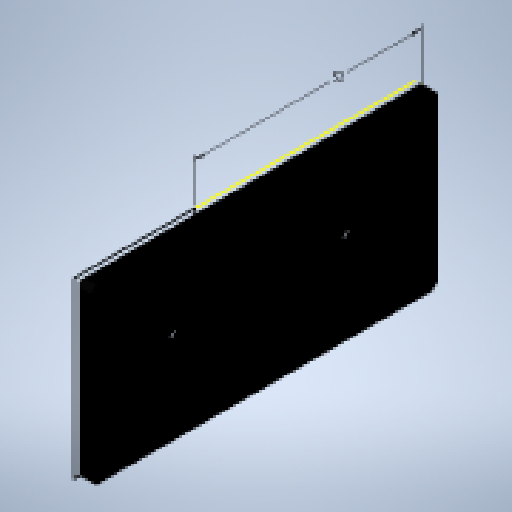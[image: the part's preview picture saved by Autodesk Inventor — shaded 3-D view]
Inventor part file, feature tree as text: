
AUTODESK INVENTOR PART (.ipt)
format: ipt  version: 2023 (Build 270158000, 158)  size: 273,920 bytes
history: native  units: mm
features: other x98, sketch x4, extrude x2, hole x2, chamfer x1
ambient origin geometry x8: Origin, YZ Plane, XZ Plane, XY Plane, X Axis, Y Axis, Z Axis, Center Point
bodies: Solid1 (feature_tree)
feature tree (107):
  extrude  "Extrusion1"  TaperAngle=0.0deg  [1 undecoded]
  hole  "Hole1"  [1 undecoded]
  hole  "Hole2"  [1 undecoded]
  other  "CS_ANBAU_CAP_XY"
  other  "CS_ANBAU_CAP_YZ"
  other  "CS_ANBAU_CAP_ZX"
  other  "CS_ANBAU_CAP_X"
  other  "CS_ANBAU_CAP_Y"
  other  "CS_ANBAU_CAP_Z"
  other  "CS_ANBAU_CAP_Center"
  other  "CS_ANBAU_CAP_90_XY"
  other  "CS_ANBAU_CAP_90_YZ"
  other  "CS_ANBAU_CAP_90_ZX"
  other  "CS_ANBAU_CAP_90_X"
  other  "CS_ANBAU_CAP_90_Y"
  other  "CS_ANBAU_CAP_90_Z"
  other  "CS_ANBAU_CAP_90_Center"
  other  "IB_1_XY"
  other  "IB_1_YZ"
  other  "IB_1_ZX"
  other  "IB_1_X"
  other  "IB_1_Y"
  other  "IB_1_Z"
  other  "IB_1_Center"
  other  "IB_10_XY"
  other  "IB_10_YZ"
  other  "IB_10_ZX"
  other  "IB_10_X"
  other  "IB_10_Y"
  other  "IB_10_Z"
  other  "IB_10_Center"
  other  "IB_11_XY"
  other  "IB_11_YZ"
  other  "IB_11_ZX"
  other  "IB_11_X"
  other  "IB_11_Y"
  other  "IB_11_Z"
  other  "IB_11_Center"
  other  "IB_12_XY"
  other  "IB_12_YZ"
  other  "IB_12_ZX"
  other  "IB_12_X"
  other  "IB_12_Y"
  other  "IB_12_Z"
  other  "IB_12_Center"
  other  "IB_2_XY"
  other  "IB_2_YZ"
  other  "IB_2_ZX"
  other  "IB_2_X"
  other  "IB_2_Y"
  other  "IB_2_Z"
  other  "IB_2_Center"
  other  "IB_3_XY"
  other  "IB_3_YZ"
  other  "IB_3_ZX"
  other  "IB_3_X"
  other  "IB_3_Y"
  other  "IB_3_Z"
  other  "IB_3_Center"
  other  "IB_4_XY"
  other  "IB_4_YZ"
  other  "IB_4_ZX"
  other  "IB_4_X"
  other  "IB_4_Y"
  other  "IB_4_Z"
  other  "IB_4_Center"
  other  "IB_5_XY"
  other  "IB_5_YZ"
  other  "IB_5_ZX"
  other  "IB_5_X"
  other  "IB_5_Y"
  other  "IB_5_Z"
  other  "IB_5_Center"
  other  "IB_6_XY"
  other  "IB_6_YZ"
  other  "IB_6_ZX"
  other  "IB_6_X"
  other  "IB_6_Y"
  other  "IB_6_Z"
  other  "IB_6_Center"
  other  "IB_7_XY"
  other  "IB_7_YZ"
  other  "IB_7_ZX"
  other  "IB_7_X"
  other  "IB_7_Y"
  other  "IB_7_Z"
  other  "IB_7_Center"
  other  "IB_8_XY"
  other  "IB_8_YZ"
  other  "IB_8_ZX"
  other  "IB_8_X"
  other  "IB_8_Y"
  other  "IB_8_Z"
  other  "IB_8_Center"
  other  "IB_9_XY"
  other  "IB_9_YZ"
  other  "IB_9_ZX"
  other  "IB_9_X"
  other  "IB_9_Y"
  other  "IB_9_Z"
  other  "IB_9_Center"
  chamfer  "Chamfer1"  [1 undecoded]
  extrude  "Extrusion2"  TaperAngle=0.0deg  [1 undecoded]
  sketch  "Skizze_1"  dims[d0=4.0mm d1=0.0mm]
  sketch  "Sketch2"  dims[d2=4.0mm d3=6.0mm d4=8.1mm d5=2.0mm d6=90.0deg d7=4.0mm d8=0.0mm]
  sketch  "Sketch3"  dims[d9=4.0mm d10=6.0mm d11=8.1mm d12=2.0mm d13=90.0deg d14=4.0mm d15=0.0mm d16=0.0mm]
  sketch  "Sketch5"  dims[d17=0.0mm d18=0.0mm d19=0.0mm d20=0.0mm d21=0.0mm d22=0.0mm d23=0.0mm d24=0.0mm d25=0.0mm d26=0.0mm d27=0.0mm d28=1.25mm d29=2.0mm d30=45.0deg d32=52.0mm d33=4.0mm d34=0.0mm]
note: 5 required parameter values undecoded (feature->parameter linkage not recoverable at this tier; creation-order binding heuristic only, values carry confidence <= 0.55)
